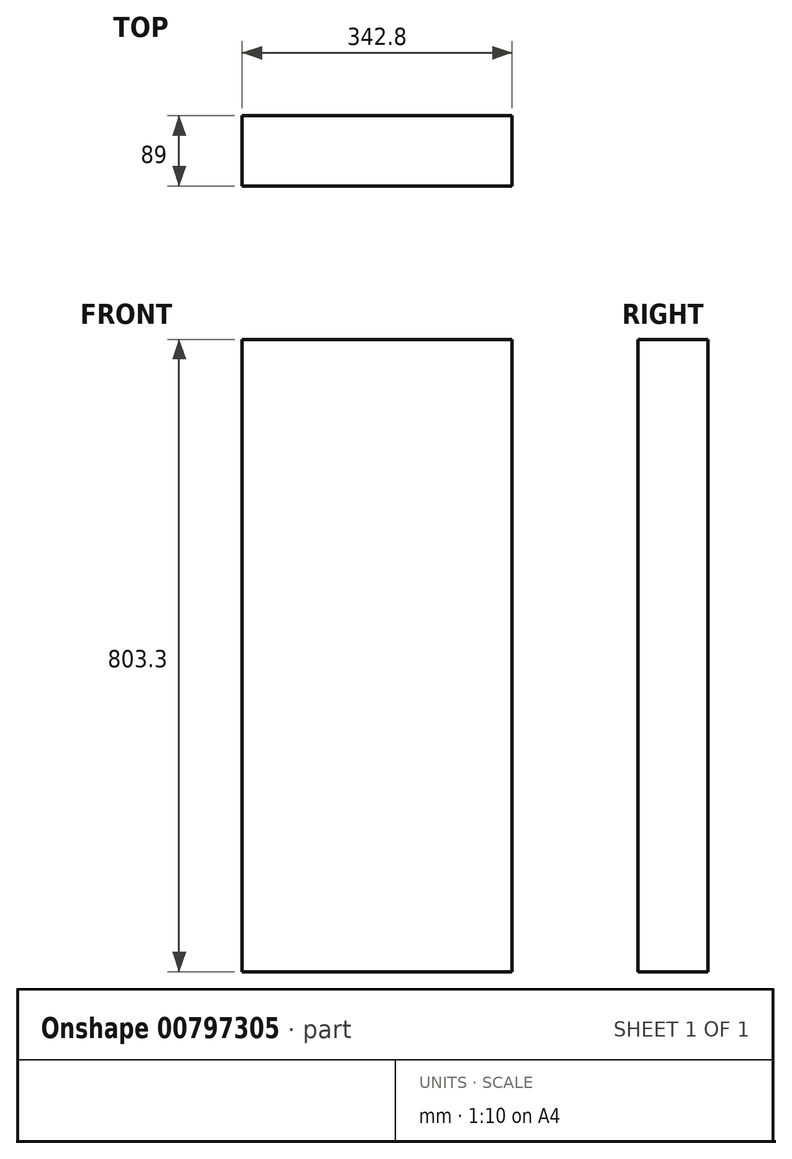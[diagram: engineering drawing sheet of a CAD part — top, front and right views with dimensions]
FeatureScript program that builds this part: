
annotation { "Feature Type Name" : "Feature", "Feature Type Description" : "" }
export const myFeature = defineFeature(function(context is Context, id is Id, definition is map)
    precondition{}
    {
        {
            var Q0;
            Q0=qCreatedBy(makeId("Front.planeOp"),FACE);
            var sketch = newSketch(context, id + "F0", { "sketchPlane" : qUnion([Q0])});
            skLineSegment(sketch, "E0.bottom", {"start": v(171.4, 401.65) * mm, "end": v(-171.4, 401.65) * mm});
            skLineSegment(sketch, "E0.top", {"start": v(171.4, -401.65) * mm, "end": v(-171.4, -401.65) * mm});
            skLineSegment(sketch, "E0.left", {"start": v(171.4, 401.65) * mm, "end": v(171.4, -401.65) * mm});
            skLineSegment(sketch, "E0.right", {"start": v(-171.4, 401.65) * mm, "end": v(-171.4, -401.65) * mm});
            skPoint(sketch, "E0.middle", {"position": v(0, 0) * mm});
            skSolve(sketch);
        }
        {
            var Q0;
            Q0 = qSketchRegion(id + "F0", true);
            extrude(context, id + "F1", {"entities" : qUnion([Q0]), "depth" : 89 * mm, "offsetDistance" : 25 * mm, "symmetric" : true});
        }
    });
